# Revit family: ALT-C128
name_source: partatom
category: Lighting Fixtures
units: mm (PartAtom-declared; Revit-internal decimal feet)

## family parameters
Always vertical = Yes
Cut with Voids When Loaded = No
Host = Ceiling
Light Source = Yes
OmniClass Number = 23.80.70.11.14.17
OmniClass Title = Direct/Indirect
Part Type = Normal
Room Calculation Point = No
Round Connector Dimension = Use Diameter
Shared = No

## types (11) — shared parameters
Assembly Code = D5020200
Color Filter = 16777215
Description = Architectural Recessed Troffer with Regressed Lens
Dimming Lamp Color Temperature Shift = <None>
Emit Shape Visible in Rendering = No
Emit from Rectangle Height = 0' - 0 1/8"
Housing Finish = Metal - Viscor - White
Lamp = LED
Lens Depth = 0' - 0 1/8"
Lens Finish = Acrylic - Viscor - Frosted White
Manufacturer = VISIONEERING by VISCOR
Model = ALT-C128
Tilt Angle = 90.00°
URL = https://www.viscor.com
Voltage = 120 V

## per-type parameters (varying)
| type | Apparent Load | Emit from Rectangle Length | Emit from Rectangle Width | Lamp Wattage | Length | Photometric Web File | Width |
| ALT2X4-LED840K070LUNV-C128 | 54 VA | 3' - 11 3/4" | 1' - 11 3/4" | 54 VA | 3' - 11 3/4" | ALT2x4-LED840K070LUNV-C128.ies | 1' - 11 3/4" |
| ALT1x4-LED840K020LUNV-C128 | 16 VA | 3' - 11 3/4" | 0' - 11 3/4" | 16 VA | 3' - 11 3/4" | ALT1x4-LED840K020LUNV-C128.ies | 0' - 11 3/4" |
| ALT2x2-LED840K024LUNV-C128 | 19 VA | 1' - 11 3/4" | 1' - 11 3/4" | 19 VA | 1' - 11 3/4" | ALT2x2-LED840K024LUNV-C128.ies | 1' - 11 3/4" |
| ALT1x4-LED840K030LUNV-C128 | 24 VA | 3' - 11 3/4" | 0' - 11 3/4" | 24 VA | 3' - 11 3/4" | ALT1x4-LED840K030LUNV-C128.ies | 0' - 11 3/4" |
| ALT1x4-LED840K040LUNV-C128 | 33 VA | 3' - 11 3/4" | 0' - 11 3/4" | 33 VA | 3' - 11 3/4" | ALT1x4-LED840K040LUNV-C128.ies | 0' - 11 3/4" |
| ALT2x2-LED840K034LUNV-C128 | 27 VA | 1' - 11 3/4" | 1' - 11 3/4" | 27 VA | 1' - 11 3/4" | ALT2x2-LED840K034LUNV-C128.ies | 1' - 11 3/4" |
| ALT2x2-LED840K040LUNV-C128 | 32 VA | 1' - 11 3/4" | 1' - 11 3/4" | 32 VA | 1' - 11 3/4" | ALT2x2-LED840K040LUNV-C128.ies | 1' - 11 3/4" |
| ALT2x2-LED840K050LUNV-C128 | 41 VA | 1' - 11 3/4" | 1' - 11 3/4" | 41 VA | 1' - 11 3/4" | ALT2x2-LED840K050LUNV-C128.ies | 1' - 11 3/4" |
| ALT2x4-LED840K036LUNV-C128 | 27 VA | 3' - 11 3/4" | 1' - 11 3/4" | 27 VA | 3' - 11 3/4" | ALT2x4-LED840K036LUNV-C128.ies | 1' - 11 3/4" |
| ALT2x4-LED840K050LUNV-C128 | 38 VA | 3' - 11 3/4" | 1' - 11 3/4" | 38 VA | 3' - 11 3/4" | ALT2x4-LED840K050LUNV-C128.ies | 1' - 11 3/4" |
| ALT2x4-LED840K060LUNV-C128 | 46 VA | 3' - 11 3/4" | 1' - 11 3/4" | 46 VA | 3' - 11 3/4" | ALT2x4-LED840K060LUNV-C128.ies | 1' - 11 3/4" |

## geometry (parser evidence)
native form markers: Sweep x2
no freeform markers — native parametric forms only
